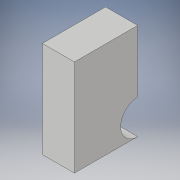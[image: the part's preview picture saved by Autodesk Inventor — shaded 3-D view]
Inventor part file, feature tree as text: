
AUTODESK INVENTOR PART (.ipt)
format: ipt  version: 2019 (Build 230136000, 136)  size: 90,112 bytes
history: native  units: in
note: dims shown in document units (in); Inventor stores cm internally (conversion verified against a paired STEP export)
features: extrude x1, sketch x1
ambient origin geometry x8: Origin, YZ Plane, XZ Plane, XY Plane, X Axis, Y Axis, Z Axis, Center Point
bodies: Solid1 (feature_tree)
feature tree (2):
  extrude  "Extrusion1"  Depth=1.0in TaperAngle=0.0deg
  sketch  "Sketch1"  dims[d0=3.0in d1=1.0in d2=0.0in]
